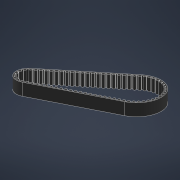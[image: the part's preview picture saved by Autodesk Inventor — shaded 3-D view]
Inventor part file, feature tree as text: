
AUTODESK INVENTOR PART (.ipt)
format: ipt  version: 2021 (Build 250183000, 183)  size: 732,160 bytes
history: native  units: in
note: dims shown in document units (in); Inventor stores cm internally (conversion verified against a paired STEP export)
features: other x7, extrude x4, pattern_circular x2, sketch x1
ambient origin geometry x8: Origin, YZ Plane, XZ Plane, XY Plane, X Axis, Y Axis, Z Axis, Center Point
bodies: Body1 (feature_tree)
feature tree (14):
  other  "top teeth placement"
  other  "htd profile"
  extrude  "Top/Left Base Tooth"  Depth=0.5906in
  other  "Top Teeth"
  other  "Pulley 1 Center"
  pattern_circular  "Left Teeth"  Count=22  [1 undecoded]
  other  "Pulley 2 Center"
  extrude  "Right Base Tooth"  Depth=0.5906in
  pattern_circular  "Right Teeth"  [2 undecoded]
  other  "bottom teeth placement"
  extrude  "Bottom Base Tooth"  Depth=0.5906in
  other  "Bottom Teeth"
  extrude  "Belt"  Depth=0.5906in
  sketch  "Sketch7"  dims[d17=1.1279in d18=2.2557in d28=8.6614in d30=0.1969in d31=0.3937in d33=0.3937in d35=4.1563in d36=1.6196in d37=0.7874in d39=0.1374in d41=0.1969in d43=0.0394in d44=0.1744in d45=3.8475in d46=0.7874in d48=0.0687in d50=0.1969in d52=0.1521in d60=0.7874in d62=0.1969in d63=0.3937in d65=0.3937in d71=4.1944in d74=0.5906in d75=0.0in d76=3.1496in d77=1.0994in d80=1.3605in d81=1.3193in d85=0.5906in d86=0.0in d87=7.4803in d88=180.0deg d93=0.0587in d94=0.0169in d95=0.0811in d97=0.1378in d98=0.1969in d99=0.0225in d101=0.1488in d102=0.0587in d103=0.0169in d104=0.0811in d105=0.1378in d106=0.1969in d107=0.1488in d108=0.1969in d109=0.0225in d120=8.2677in d122=0.3937in d123=1.1279in d124=2.2557in d126=4.1563in d127=1.6196in d131=3.8475in d134=0.1521in d135=0.1969in d136=4.1944in d140=0.3937in d144=0.1969in d145=7.0866in d146=14.1732in d147=1.5748in d150=0.0587in d151=0.0169in d152=0.0811in d153=0.1378in d154=0.1969in d155=0.1488in d156=0.1969in d157=0.0225in d158=0.5906in d159=0.0in d160=0.5906in d161=0.0in d163=0.1496in d111=0.0197in d112=0.0344in d113=0.0197in d114=0.0344in]
note: 3 required parameter values undecoded (feature->parameter linkage not recoverable at this tier; creation-order binding heuristic only, values carry confidence <= 0.55)
